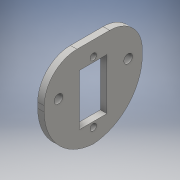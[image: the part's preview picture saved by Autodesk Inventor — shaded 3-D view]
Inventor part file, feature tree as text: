
AUTODESK INVENTOR PART (.ipt)
format: ipt  version: 2016 (Build 200138000, 138)  size: 136,704 bytes
history: native  units: mm
features: extrude x2, sketch x1
ambient origin geometry x8: Origin, YZ Plane, XZ Plane, XY Plane, X Axis, Y Axis, Z Axis, Center Point
bodies: Solid1 (feature_tree)
feature tree (3):
  extrude  "Extrusion1"  Depth=45.0mm
  extrude  "Extrusion11"  Depth=12.5mm
  sketch  "Sketch11"  dims[d0=41.5mm d1=45.0mm d3=12.5mm d4=23.5mm d5=16.25mm d6=3.0mm d7=2.25mm d8=2.25mm d9=3.0mm d10=0.0mm d30=3.0mm d31=6.75mm d32=22.5mm d33=22.5mm d55=15.5mm d56=16.0mm d57=4.0mm d58=4.0mm d60=15.5mm d61=16.0mm d62=15.0mm d63=24.0mm d64=10.0mm d65=0.0mm]
